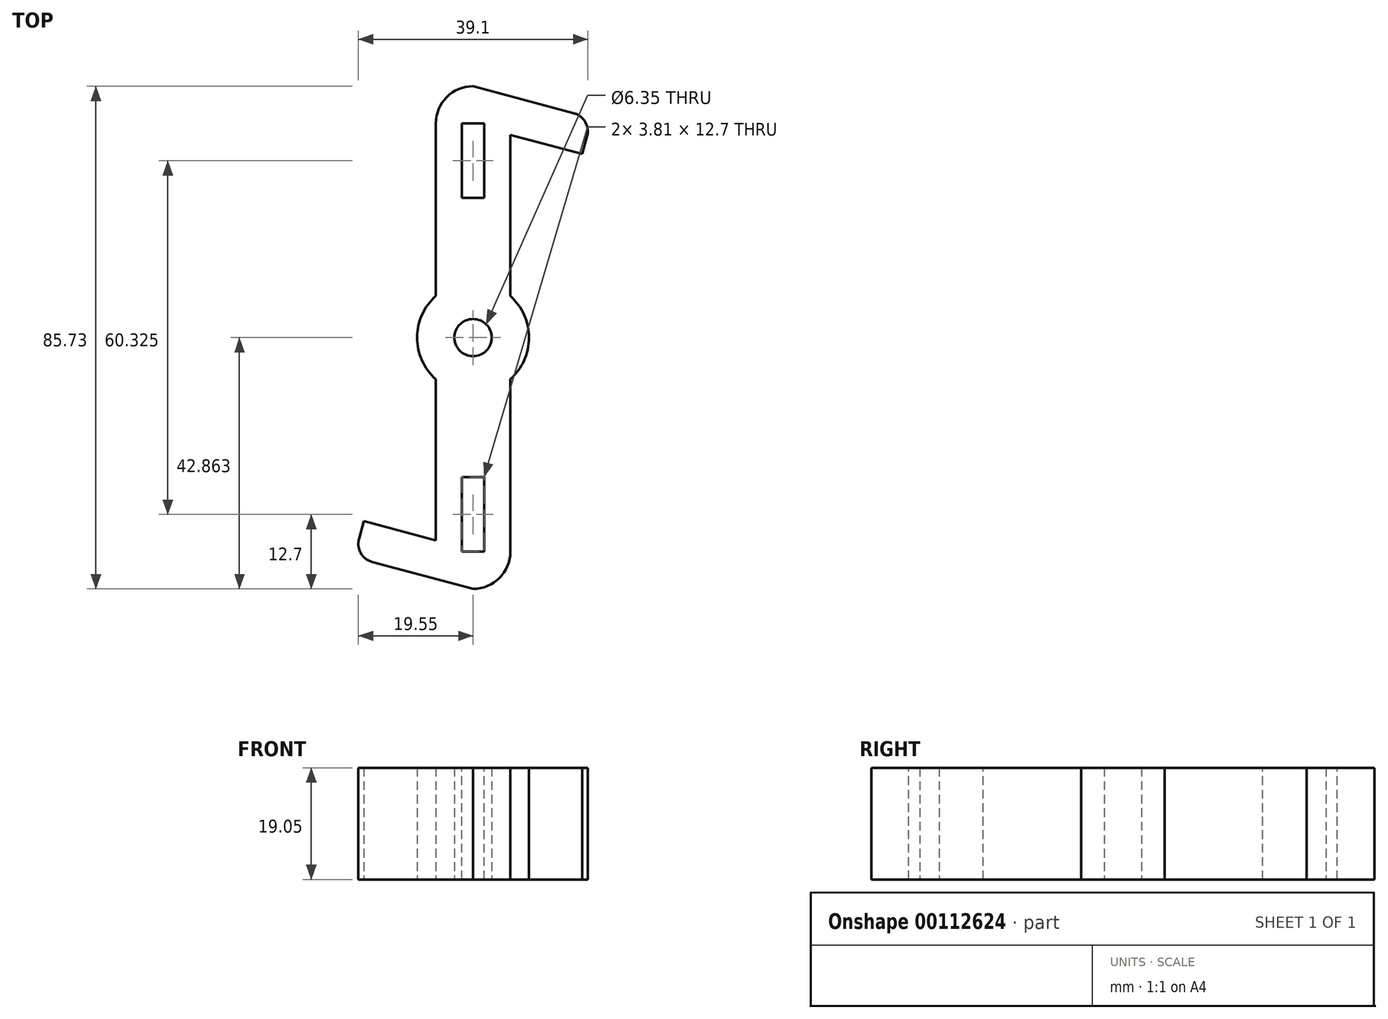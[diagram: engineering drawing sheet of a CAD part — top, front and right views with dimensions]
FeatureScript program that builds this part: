
annotation { "Feature Type Name" : "Feature", "Feature Type Description" : "" }
export const myFeature = defineFeature(function(context is Context, id is Id, definition is map)
    precondition{}
    {
        {
            var Q0;
            Q0=qCreatedBy(makeId("Top.planeOp"),FACE);
            var sketch = newSketch(context, id + "F0", { "sketchPlane" : qUnion([Q0])});
            skLineSegment(sketch, "E0.bottom", {"start": v(0, 0) * mm, "end": v(12.7, 0) * mm, "construction": true});
            skLineSegment(sketch, "E0.top", {"start": v(0, 73.03) * mm, "end": v(12.7, 73.03) * mm, "construction": true});
            skLineSegment(sketch, "E0.left", {"start": v(0, 0) * mm, "end": v(0, 73.03) * mm, "construction": true});
            skArc(sketch, "E1", {"start": v(12.7, 73.03) * mm, "mid": v(6.35, 79.38) * mm, "end": v(0, 73.03) * mm, "construction": true});
            skArc(sketch, "E2", {"start": v(0, 0) * mm, "mid": v(6.35, -6.35) * mm, "end": v(12.7, 0) * mm, "construction": true});
            skLineSegment(sketch, "E3", {"start": v(0, 36.51) * mm, "end": v(12.7, 36.51) * mm, "construction": true});
            skCircle(sketch, "E4", {"center": v(6.35, 36.51) * mm, "radius": 9.53 * mm});
            skLineSegment(sketch, "E5", {"start": v(0, 73.03) * mm, "end": v(0, 43.61) * mm});
            skLineSegment(sketch, "E6", {"start": v(12.7, 29.41) * mm, "end": v(12.7, 0) * mm});
            skCircle(sketch, "E7", {"center": v(6.35, 36.51) * mm, "radius": 3.18 * mm});
            skArc(sketch, "E8", {"start": v(6.35, 79.38) * mm, "mid": v(1.86, 77.52) * mm, "end": v(0, 73.03) * mm});
            skLineSegment(sketch, "E9", {"start": v(6.35, 79.37) * mm, "end": v(26.61, 73.95) * mm, "construction": true});
            skLineSegment(sketch, "E10", {"start": v(26.61, 73.95) * mm, "end": v(24.97, 67.81) * mm, "construction": true});
            skLineSegment(sketch, "E11", {"start": v(24.97, 67.81) * mm, "end": v(12.7, 71.1) * mm});
            skLineSegment(sketch, "E12", {"start": v(12.7, 73.03) * mm, "end": v(12.7, 0) * mm, "construction": true});
            skLineSegment(sketch, "E13", {"start": v(12.7, 71.1) * mm, "end": v(12.7, 43.61) * mm});
            skArc(sketch, "E14", {"start": v(25.79, 70.88) * mm, "mid": v(25.47, 73.29) * mm, "end": v(23.54, 74.77) * mm});
            skLineSegment(sketch, "E15", {"start": v(25.79, 70.88) * mm, "end": v(24.97, 67.81) * mm});
            skLineSegment(sketch, "E16", {"start": v(23.54, 74.77) * mm, "end": v(6.35, 79.38) * mm});
            skArc(sketch, "E17", {"start": v(6.35, -6.35) * mm, "mid": v(10.84, -4.5) * mm, "end": v(12.7, 0) * mm});
            skLineSegment(sketch, "E18", {"start": v(6.35, -6.35) * mm, "end": v(-13.91, -0.92) * mm, "construction": true});
            skLineSegment(sketch, "E19", {"start": v(-13.91, -0.92) * mm, "end": v(-12.27, 5.21) * mm, "construction": true});
            skLineSegment(sketch, "E20", {"start": v(-12.27, 5.21) * mm, "end": v(0, 1.93) * mm});
            skArc(sketch, "E21", {"start": v(-13.09, 2.15) * mm, "mid": v(-12.77, -0.26) * mm, "end": v(-10.84, -1.74) * mm});
            skLineSegment(sketch, "E22", {"start": v(-13.09, 2.15) * mm, "end": v(-12.27, 5.21) * mm});
            skLineSegment(sketch, "E23", {"start": v(-10.84, -1.74) * mm, "end": v(6.35, -6.35) * mm});
            skLineSegment(sketch, "E24", {"start": v(0, 1.93) * mm, "end": v(0, 29.41) * mm});
            skSolve(sketch);
        }
        {
            var Q0;
            Q0 = qSketchRegion(id + "F0", true);
            extrude(context, id + "F1", {"entities" : qUnion([Q0]), "depth" : 19.05 * mm});
        }
        {
            var Q0;
            Q0=makeQuery(id+"F1.opExtrude","CAP_FACE",FACE,{"disambiguationData":[OSD([sQuery(id+"F0.wireOp",EDGE,"E1"),sQuery(id+"F0.wireOp",EDGE,"E2"),sQuery(id+"F0.wireOp",EDGE,"E4"),sQuery(id+"F0.wireOp",EDGE,"FbjBpS19-E62y-OzMl-BGLg-Xct3kmr7IAPC"),sQuery(id+"F0.wireOp",EDGE,"E5"),sQuery(id+"F0.wireOp",EDGE,"ejdmprwq-hUIN-6rnX-YKVA-hAiSx6FL2sLM"),sQuery(id+"F0.wireOp",EDGE,"E6"),sQuery(id+"F0.wireOp",EDGE,"E7")])],"isStart":false});
            var sketch = newSketch(context, id + "F2", { "sketchPlane" : qUnion([Q0])});
            skLineSegment(sketch, "E25", {"start": v(0, 73.03) * mm, "end": v(12.7, 73.03) * mm, "construction": true});
            skLineSegment(sketch, "E26.bottom", {"start": v(4.44, 73.03) * mm, "end": v(8.25, 73.03) * mm});
            skLineSegment(sketch, "E26.top", {"start": v(4.44, 60.33) * mm, "end": v(8.25, 60.33) * mm});
            skLineSegment(sketch, "E26.left", {"start": v(4.44, 73.03) * mm, "end": v(4.44, 60.33) * mm});
            skLineSegment(sketch, "E26.right", {"start": v(8.25, 73.03) * mm, "end": v(8.25, 60.33) * mm});
            skPoint(sketch, "E27", {"position": v(6.35, 73.03) * mm});
            skLineSegment(sketch, "E28", {"start": v(0, 0) * mm, "end": v(12.7, 0) * mm, "construction": true});
            skLineSegment(sketch, "E29.bottom", {"start": v(4.45, 12.7) * mm, "end": v(8.25, 12.7) * mm});
            skLineSegment(sketch, "E29.top", {"start": v(4.45, 0) * mm, "end": v(8.26, 0) * mm});
            skLineSegment(sketch, "E29.left", {"start": v(4.45, 12.7) * mm, "end": v(4.45, 0) * mm});
            skLineSegment(sketch, "E29.right", {"start": v(8.26, 12.7) * mm, "end": v(8.26, 0) * mm});
            skPoint(sketch, "E30", {"position": v(6.35, 0) * mm});
            skLineSegment(sketch, "E31", {"start": v(12.7, 71.1) * mm, "end": v(12.7, 77.67) * mm, "construction": true});
            skLineSegment(sketch, "E32", {"start": v(0, 1.93) * mm, "end": v(0, -4.65) * mm, "construction": true});
            skSolve(sketch);
        }
        {
            var Q0;
            Q0 = qSketchRegion(id + "F2", true);
            var Q1;
            Q1=makeQuery(id+"F1.opExtrude","CAP_FACE",FACE,{"disambiguationData":[OSD([sQuery(id+"F0.wireOp",EDGE,"E1"),sQuery(id+"F0.wireOp",EDGE,"E2"),sQuery(id+"F0.wireOp",EDGE,"E4"),sQuery(id+"F0.wireOp",EDGE,"FbjBpS19-E62y-OzMl-BGLg-Xct3kmr7IAPC"),sQuery(id+"F0.wireOp",EDGE,"E5"),sQuery(id+"F0.wireOp",EDGE,"ejdmprwq-hUIN-6rnX-YKVA-hAiSx6FL2sLM"),sQuery(id+"F0.wireOp",EDGE,"E6"),sQuery(id+"F0.wireOp",EDGE,"E7")])],"isStart":true});
            extrude(context, id + "F3", {"entities" : qUnion([Q0]), "operationType" : NewBodyOperationType.REMOVE, "endBound" : BoundingType.UP_TO_SURFACE, "oppositeDirection" : true, "endBoundEntityFace" : qUnion([Q1]), "depth" : 3.8 * mm});
        }
    });
